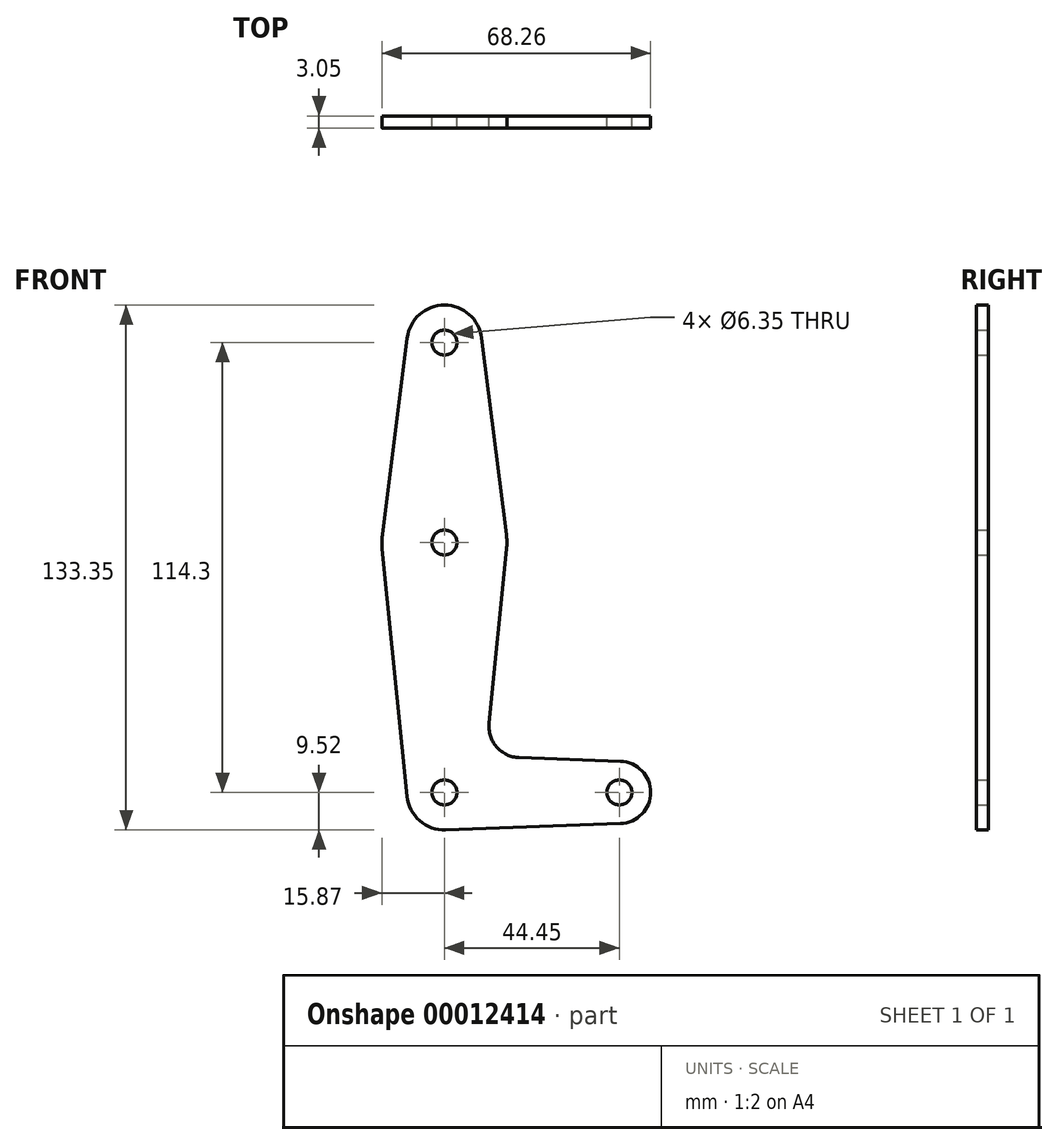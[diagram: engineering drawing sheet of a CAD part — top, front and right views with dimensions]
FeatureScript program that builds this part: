
annotation { "Feature Type Name" : "Feature", "Feature Type Description" : "" }
export const myFeature = defineFeature(function(context is Context, id is Id, definition is map)
    precondition{}
    {
        {
            var Q0;
            Q0=qCreatedBy(makeId("Front.planeOp"),FACE);
            var sketch = newSketch(context, id + "F0", { "sketchPlane" : qUnion([Q0])});
            skLineSegment(sketch, "E0", {"start": v(0, 0) * mm, "end": v(0, 114.3) * mm, "construction": true});
            skLineSegment(sketch, "E1", {"start": v(0, 0) * mm, "end": v(44.45, 0) * mm, "construction": true});
            skCircle(sketch, "E2", {"center": v(0, 0) * mm, "radius": 9.53 * mm});
            skCircle(sketch, "E3", {"center": v(44.45, 0) * mm, "radius": 7.94 * mm});
            skCircle(sketch, "E4", {"center": v(0, 63.5) * mm, "radius": 15.88 * mm});
            skCircle(sketch, "E5", {"center": v(0, 114.3) * mm, "radius": 9.53 * mm});
            skLineSegment(sketch, "E6", {"start": v(-9.45, 115.5) * mm, "end": v(-15.75, 65.48) * mm});
            skLineSegment(sketch, "E7", {"start": v(9.45, 115.5) * mm, "end": v(15.75, 65.48) * mm});
            skLineSegment(sketch, "E8", {"start": v(15.8, 61.91) * mm, "end": v(11.34, 17.6) * mm});
            skLineSegment(sketch, "E9", {"start": v(-15.8, 61.91) * mm, "end": v(-9.48, -0.95) * mm});
            skLineSegment(sketch, "E10", {"start": v(18.97, 8.85) * mm, "end": v(44.73, 7.93) * mm});
            skLineSegment(sketch, "E11", {"start": v(0.34, -9.52) * mm, "end": v(44.73, -7.93) * mm});
            skCircle(sketch, "E12", {"center": v(0, 114.3) * mm, "radius": 3.18 * mm});
            skCircle(sketch, "E13", {"center": v(0, 63.5) * mm, "radius": 3.18 * mm});
            skCircle(sketch, "E14", {"center": v(0, 0) * mm, "radius": 3.18 * mm});
            skCircle(sketch, "E15", {"center": v(44.45, 0) * mm, "radius": 3.18 * mm});
            skArc(sketch, "E16.filletArc", {"start": v(11.34, 17.6) * mm, "mid": v(13.26, 11.57) * mm, "end": v(18.97, 8.85) * mm});
            skSolve(sketch);
        }
        {
            var Q0;
            Q0 = qSketchRegion(id + "F0", true);
            extrude(context, id + "F1", {"entities" : qUnion([Q0]), "depth" : 3.05 * mm});
        }
    });
